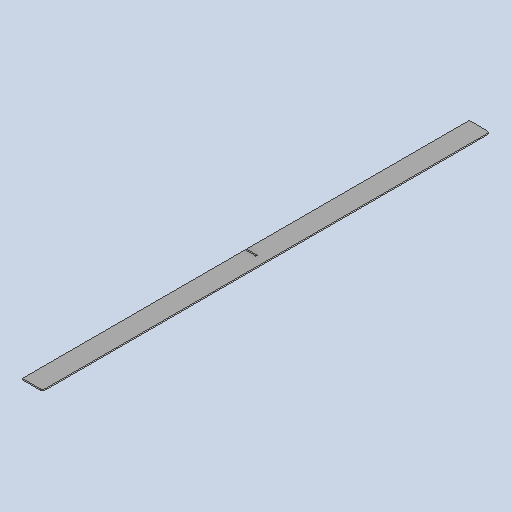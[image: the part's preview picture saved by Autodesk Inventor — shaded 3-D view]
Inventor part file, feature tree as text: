
AUTODESK INVENTOR PART (.ipt)
format: ipt  version: 2025 (Build 290162010, 162A)  size: 127,488 bytes
history: native  units: mm
features: other x3, sheet_metal_op x1, chamfer x1, sketch x1
ambient origin geometry x8: Origin, YZ Plane, XZ Plane, XY Plane, X Axis, Y Axis, Z Axis, Center Point
bodies: Body1 (feature_tree)
feature tree (6):
  other  "BSH 506 amplifier"
  sheet_metal_op  "Face2"
  chamfer  "Corner Round2"
  sketch  "Sketch1"  dims[d15=3.0mm d17=1098.0mm d18=50.0mm d19=3.0mm d20=26.0mm d22=6.0mm]
  other  "Plate2"
  other  "Definition1"
